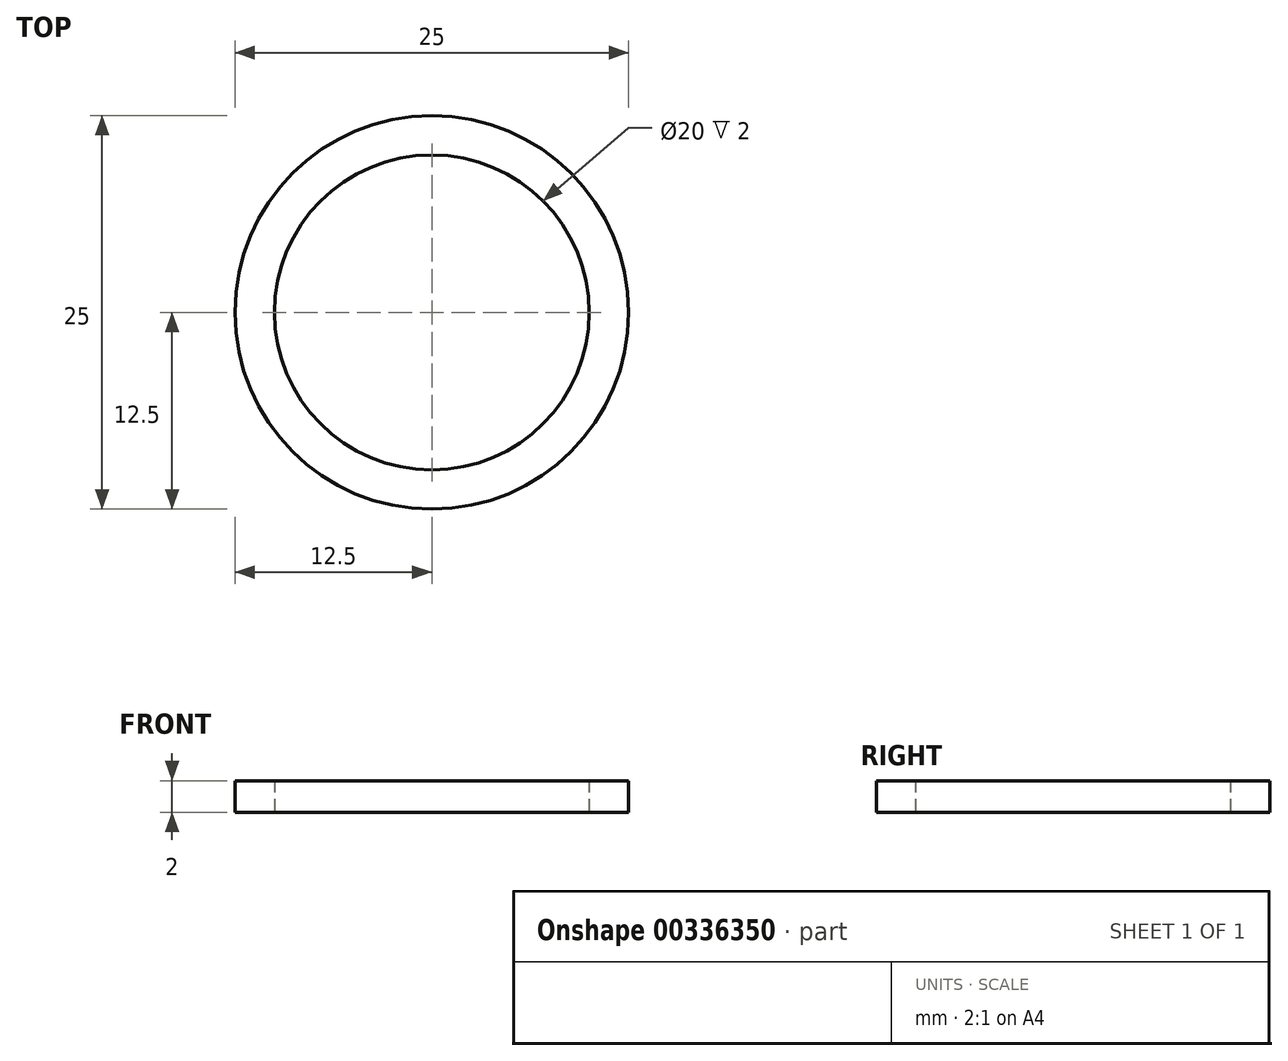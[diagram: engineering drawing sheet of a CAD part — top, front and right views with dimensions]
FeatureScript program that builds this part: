
annotation { "Feature Type Name" : "Feature", "Feature Type Description" : "" }
export const myFeature = defineFeature(function(context is Context, id is Id, definition is map)
    precondition{}
    {
        {
            var Q0;
            Q0=qCreatedBy(makeId("Top.planeOp"),FACE);
            var sketch = newSketch(context, id + "F0", { "sketchPlane" : qUnion([Q0])});
            skCircle(sketch, "E0", {"center": v(0, 0) * mm, "radius": 10 * mm});
            skCircle(sketch, "E1", {"center": v(0, 0) * mm, "radius": 12.5 * mm});
            skSolve(sketch);
        }
        {
            var Q0;
            Q0 = qSketchRegion(id + "F0", true);
            extrude(context, id + "F1", {"entities" : qUnion([Q0]), "depth" : 2 * mm});
        }
    });
